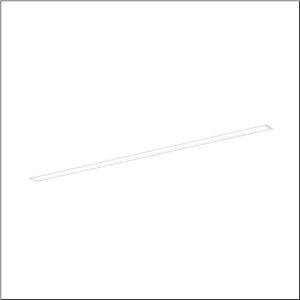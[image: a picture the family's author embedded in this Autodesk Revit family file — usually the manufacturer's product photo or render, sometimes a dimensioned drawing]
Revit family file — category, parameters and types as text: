
# Revit family: silica_r__21_51mx13db45wb_7b80
name_source: partatom
category: Lighting Fixtures
units: mm (PartAtom-declared; Revit-internal decimal feet)

## family parameters
Cut with Voids When Loaded = No
Host = Face
Light Source = No
Part Type = Normal
Room Calculation Point = No
Round Connector Dimension = Use Diameter
Shared = No

## types (1)
- --- (1 x LED, 4100 lm, 28.1 W, 4000K)
    Apparent Load = 28 VA
    CIE Flux Codes = 78 96 99 100 100
    Color Rendering = 80
    Color Temperature = 4000K
    Default Elevation = 1800 mm
    Description = Silica® 21, office luminaire, primary optical cover: prismatic diffuser, of PMMA, CAT 2 (L<= 3000cd/m²), light emission: direct distribution, primary light characteristic: symmetric, installation type: recessed, LED, rated luminous flux: 4.100lm, luminous efficacy: 146lm/W, light colour: 840, colour temperature: 4000K, with terminal, 3+2-pole, max. 2.5mm², mains connection: 220..240V, AC, 50/60Hz, rated input power: 28.1W, luminaire housing, of aluminium, traffic white (RAL 9016), length: 1.528mm, width: 79mm, height: 53mm, protection rating (complete): IP20, insulation class (complete): insulation class I (protective earthing), certification: CE, permissible operating ambient temperature: 0..+35°C, standard: EN 50419, packaging unit: 1 piece
    Height = 0 mm  [stored 0 ft]
    Lamp = 1 x LED
    Lamp Light Flux = 4100 lm
    Lamp Power = 28.1 W
    Lamp count = 1
    Length = 1527 mm
    Luminous efficacy = 146 lm/W
    Manufacturer = Siteco
    ModVariant = No
    Model = 51MX13DB45WB
    Mounting Place = Ceiling
    Mounting Type = Recessed
    Number of Poles = 1
    OnlyDefault = Yes
    Power Factor = 1
    Product Name = Silica® 21
    Product group = office luminaire | ceiling recessed
    ProductGroupID = 401
    Protection Class = Protection class I
    Protection Degree = IP 20
    RLX_Detail_Level = 1
    RLX_Emergency_Light_Flux = 0 lm
    RLX_Emergency_Type = 0
    RLX_Emergency_Type_DB = No
    RlxData = <blob elided: 14297 chars, md5=70cc3fa6>
    Socket = socket
    Standby Power = 0 W
    System Light Flux = 4100 lm
    System Power = 28 W
    Type Comments = factory setting: luminous flux: 100 % | dim-lin: 254 | 323 mA
    Type Image = l_1251692.jpg
    URL = http://relux.com
    VarID = @adj_049445
    Voltage = 0 V
    Weight = 0.00 kg
    Width = 79 mm

note: [stored X ft] marks values corroborated as IEEE doubles in the binary element streams (Revit-internal decimal feet)

## geometry (parser evidence)
native form markers: Sweep x12
no freeform markers — native parametric forms only
